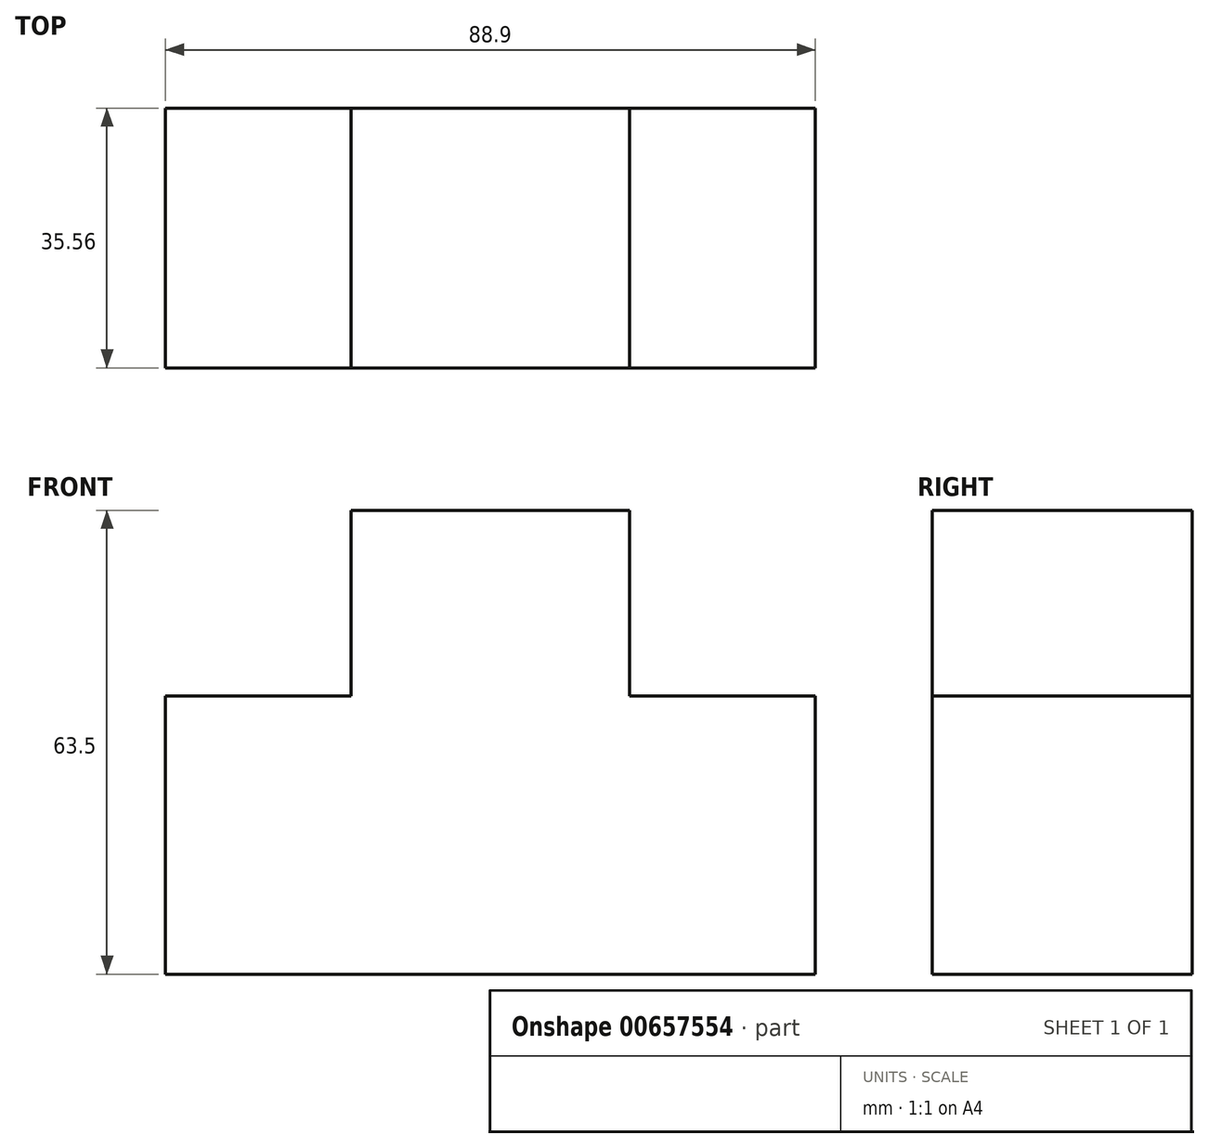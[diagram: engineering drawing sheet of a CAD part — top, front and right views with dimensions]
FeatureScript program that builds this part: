
annotation { "Feature Type Name" : "Feature", "Feature Type Description" : "" }
export const myFeature = defineFeature(function(context is Context, id is Id, definition is map)
    precondition{}
    {
        {
            var Q0;
            Q0=qCreatedBy(makeId("Front.planeOp"),FACE);
            var sketch = newSketch(context, id + "F0", { "sketchPlane" : qUnion([Q0])});
            skLineSegment(sketch, "E0", {"start": v(-42.02, -34.58) * mm, "end": v(46.88, -34.58) * mm});
            skLineSegment(sketch, "E1", {"start": v(46.88, -34.58) * mm, "end": v(46.88, 3.52) * mm});
            skLineSegment(sketch, "E2", {"start": v(46.88, 3.52) * mm, "end": v(21.48, 3.52) * mm});
            skLineSegment(sketch, "E3", {"start": v(21.48, 3.52) * mm, "end": v(21.48, 28.92) * mm});
            skLineSegment(sketch, "E4", {"start": v(21.48, 28.92) * mm, "end": v(-16.62, 28.92) * mm});
            skLineSegment(sketch, "E5", {"start": v(-16.62, 28.92) * mm, "end": v(-16.62, 3.52) * mm});
            skLineSegment(sketch, "E6", {"start": v(-16.62, 3.52) * mm, "end": v(-42.02, 3.52) * mm});
            skLineSegment(sketch, "E7", {"start": v(-42.02, 3.52) * mm, "end": v(-42.02, -34.58) * mm});
            skSolve(sketch);
        }
        {
            var Q0;
            Q0 = qSketchRegion(id + "F0", true);
            extrude(context, id + "F1", {"entities" : qUnion([Q0]), "depth" : 35.56 * mm, "offsetDistance" : 25.4 * mm});
        }
    });
